# Revit family: knockdown 90 degree 12 pp
name_source: partatom
category: Specialty Equipment
revit_build: Autodesk Revit 2015 (Build: 20140606_1530(x64)
units: mm (PartAtom-declared; Revit-internal decimal feet)

## types (1)
- 12" Knockdown Corner Form 90-Degree
    Air Infiltration Rate = 0
    BIMobject category = External Walls
    BIMobject category code = walls-external
    BIMobject main category = Walls
    BIMobject main category code = walls
    Behavior (Isotropic, Orthotropic, Transverse Isotropic) = Isotropic
    Behavior (Isotropic, Ortothropic) = Isotropic
    Brand url = http://buildblock.com
    Concrete Volume Per Unit = 0.07 CY
    Core Width = 12"
    Default Elevation = 48"
    Density = 1.50 lb/ft³
    Description = BuildBlock Insulating Concrete Forms
    Design country = United States
    Edition number = 1
    Electrical Resistivity = 4E+15  Ω*m
    Emissivity = 0.95
    Fire Rating = 4
    Foam Material = Expanded_Polystyrene-BuildBlock-White
    Height = 16"
    Installation instructions = http://buildblock.com
    Keywords = icf, buildblock, concrete forms, insulated concrete
    Length = 48"
    Manufacturer = BuildBlock Building Systems LLC
    Manufacturer country = United States
    Manufacturer name = BuildBlock Building Systems, LLC
    Masterformat 2014 Code = 03 11 19
    Masterformat 2014 Description = Insulating Concrete Forming
    Mechanical Density = 1.50 lb/ft³
    Model = 12" Knockdown Corner Form 90-Degree
    Name = BuildBlock ICF
    Nominal height = 16"
    Nominal width = 0"
    OmniClass Code = 23-13 31 17 17
    OmniClass Description = Insulated Concrete Forms
    Permeability = 3.4869 gr/(h·ft²·inHg)
    Poisson's Ratio = 0.28
    Porosity = 0.01
    Product Guid = 806fa39a-678c-4744-bde1-e709289128ca
    Product SKU = buildlock-knockdown-90-degree-corners-12
    Product certification = http://buildblock.com
    Product data url = https://bimobject.com
    Product family = Building materials
    Product group = External wall systems
    Product url = http://buildblock.com
    QR code = http://bimobject.com
    R Value = 22
    Reflectivity = 0
    STC Rating = 54
    Shear Modulus = 3.99 ksi
    Specific Heat = 0.3511 BTU/(lb·°F)
    Subclass = Value
    Technical description = http://buildblock.com
    Tensile Strength = 0.16 ksi
    Thermal Conductivity = 0.0202 BTU/(h·ft·°F)
    Thermal Expansion Coefficient = 0.00007 1/°F
    Ties Material = Polypropylene_(Recycled)-Buildblock-Black
    Type = Solid
    UNSPSC Code = 3013
    URL = http://buildblock.com
    Uniclass 1.4 Code = L32233
    Uniclass 1.4 Description = Insulated blocks
    Uniclass 2.0 Code = SS-25-25
    Uniclass 2.0 Description = Wall Lining Systems
    Uniclass 2015 Code = Pr_20_93_52_42
    Uniclass 2015 Name = Insulated concrete blocks
    Uniformat II Code = B2010
    Uniformat II Description = Exterior Walls
    Width = 11"
    Yield Strength = 0.13 ksi
    Young's Modulus = 0.63 ksi
    Youtube clip = https://youtu.be

## geometry (parser evidence)
native form markers: Sweep x7
no freeform markers — native parametric forms only
